# Revit family: M_Valve_Balancing and Control_MEPcontent_Oventrop_Hydrocontrol VFR 10623 DN 200
name_source: partatom
category: Pipe Accessories
revit_build: Autodesk Revit 2015 (Build: 20140223_1515(x64)
units: mm (PartAtom-declared; Revit-internal decimal feet)

## types (1)
- DN 200
    Angle = 60.00°
    Angle 2 = 30.00°
    Angle 3 = -60.00°
    Article Description = Balancing valve with flanges according to DIN, PN 16
    Article Type = Hydrocontrol VFR 10623 DN 200
    Black = Color RGB 35-35-35
    Bronze = Color RGB 156-122-90
    Content Supplier URL = www.mepcontent.eu
    CurDst = 67 mm
    Custom = No
    Description = Balancing valve with flanges according to DIN, PN 16
    Dst1 = 68 mm
    DstChk = 68 mm
    EMCS Version = 2.0
    ETIM Article Class = EC011463
    Family Version = 10.14
    FlangeDiameter = 340 mm  [stored 1.11549 ft]
    GTIN = 4026755252422
    H = 473 mm  [stored 1.55184 ft]
    Hb1 = 460 mm
    Hb2 = 290 mm
    Hb3 = 48 mm
    Hb4 = 110 mm  [stored 0.360892 ft]
    Hb5 = 10 mm  [stored 0.0328084 ft]
    Hb6 = 218 mm
    Height = 467 mm  [stored 1.53215 ft]
    Hlp1 = 56 mm  [stored 0.183727 ft]
    Hlp2 = 22 mm  [stored 0.0721785 ft]
    IFCExportAs = IfcValveType
    IFCExportType = PRESSUREREDUCING
    K = 295 mm  [stored 0.967848 ft]
    L2 = 67 mm
    Length = 600 mm  [stored 1.9685 ft]
    Lgt1 = 2 mm  [stored 0.00656168 ft]
    Lgt2 = 20 mm  [stored 0.0656168 ft]
    Lgt3 = 59 mm
    Lgt4 = 217 mm  [stored 0.711942 ft]
    MEPcontent Class = VALVE_BALANCING
    Manufacturer = Oventrop
    Manufacturer Art. No. = 1062356
    Manufacturer URL = http://www.oventrop.de
    Model = Hydrocontrol VFR 10623 DN 200
    NominalDiameter = 200 mm
    NominalRadius = 100 mm
    OuterDiameter = 219 mm
    Pressure Drop = 0.0 Pa
    Product Line = Oventrop
    R1 = 9 mm  [stored 0.0295276 ft]
    R2 = 10 mm  [stored 0.0328084 ft]
    Rad1 = 148 mm
    Rad2 = 170 mm  [stored 0.557743 ft]
    Rad3 = 119 mm
    Rad4 = 116 mm
    Rad5 = 156 mm  [stored 0.511811 ft]
    Rad6 = 146 mm  [stored 0.479003 ft]
    Rad7 = 160 mm  [stored 0.524934 ft]
    RegulatorRadius = 150 mm
    Revit Version = 2015
    URL = www.stabiplan.com
    VDst = 54 mm
    VHth = 126 mm
    r1 = 2 mm  [stored 0.00656168 ft]
    r2 = 3 mm  [stored 0.00984252 ft]

note: [stored X ft] marks values corroborated as IEEE doubles in the binary element streams (Revit-internal decimal feet)

## geometry (parser evidence)
native form markers: Blend x2, Sweep x2
no freeform markers — native parametric forms only
